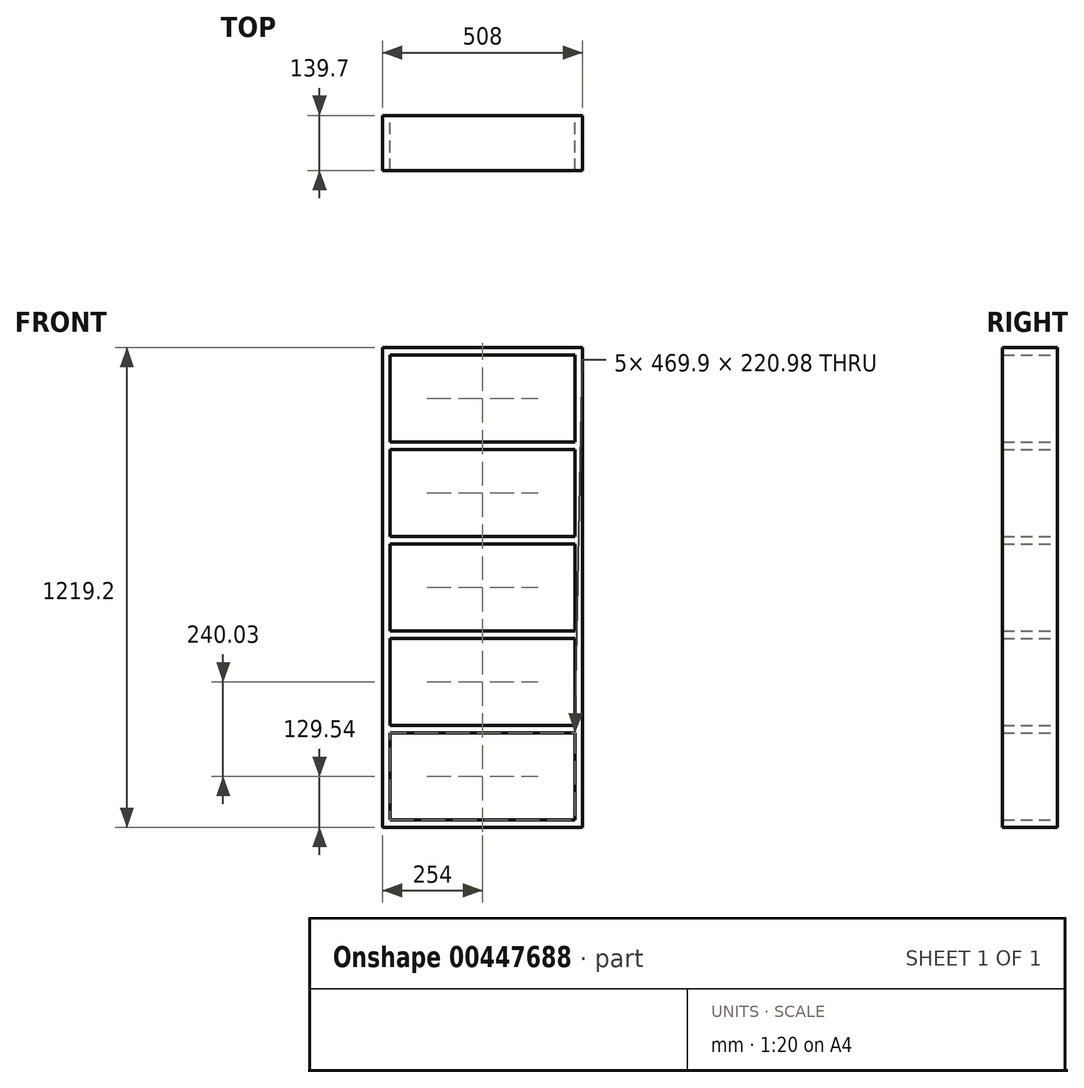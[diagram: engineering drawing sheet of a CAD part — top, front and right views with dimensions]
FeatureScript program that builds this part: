
annotation { "Feature Type Name" : "Feature", "Feature Type Description" : "" }
export const myFeature = defineFeature(function(context is Context, id is Id, definition is map)
    precondition{}
    {
        {
            var Q0;
            Q0=qCreatedBy(makeId("Front.planeOp"),FACE);
            var sketch = newSketch(context, id + "F0", { "sketchPlane" : qUnion([Q0])});
            skLineSegment(sketch, "E0.bottom", {"start": v(-254, 609.6) * mm, "end": v(254, 609.6) * mm});
            skLineSegment(sketch, "E0.top", {"start": v(-254, -609.6) * mm, "end": v(254, -609.6) * mm});
            skLineSegment(sketch, "E0.left", {"start": v(-254, 609.6) * mm, "end": v(-254, -609.6) * mm});
            skLineSegment(sketch, "E0.right", {"start": v(254, 609.6) * mm, "end": v(254, -609.6) * mm});
            skLineSegment(sketch, "E1.0", {"start": v(-234.95, 590.55) * mm, "end": v(234.95, 590.55) * mm});
            skLineSegment(sketch, "E2.0", {"start": v(234.95, 590.55) * mm, "end": v(234.95, -590.55) * mm});
            skLineSegment(sketch, "E3.0", {"start": v(-234.95, 590.55) * mm, "end": v(-234.95, -590.55) * mm});
            skLineSegment(sketch, "E4.0", {"start": v(-234.95, -590.55) * mm, "end": v(234.95, -590.55) * mm});
            skSolve(sketch);
        }
        {
            var Q0;
            Q0 = qSketchRegion(id + "F0", true);
            extrude(context, id + "F1", {"entities" : qUnion([Q0]), "depth" : 139.7 * mm});
        }
        {
            var Q0;
            Q0=qCreatedBy(makeId("Front.planeOp"),FACE);
            var sketch = newSketch(context, id + "F2", { "sketchPlane" : qUnion([Q0])});
            skLineSegment(sketch, "E5.bottom", {"start": v(-234.95, 369.57) * mm, "end": v(234.95, 369.57) * mm});
            skLineSegment(sketch, "E5.top", {"start": v(-234.95, 350.52) * mm, "end": v(234.95, 350.52) * mm});
            skLineSegment(sketch, "E5.left", {"start": v(-234.95, 369.57) * mm, "end": v(-234.95, 350.52) * mm});
            skLineSegment(sketch, "E5.right", {"start": v(234.95, 369.57) * mm, "end": v(234.95, 350.52) * mm});
            skLineSegment(sketch, "E6.bottom", {"start": v(-234.95, -110.49) * mm, "end": v(234.95, -110.49) * mm});
            skLineSegment(sketch, "E6.top", {"start": v(-234.95, -129.54) * mm, "end": v(234.95, -129.54) * mm});
            skLineSegment(sketch, "E6.left", {"start": v(-234.95, -110.49) * mm, "end": v(-234.95, -129.54) * mm});
            skLineSegment(sketch, "E6.right", {"start": v(234.95, -110.49) * mm, "end": v(234.95, -129.54) * mm});
            skLineSegment(sketch, "E7.bottom", {"start": v(-234.95, 129.54) * mm, "end": v(234.95, 129.54) * mm});
            skLineSegment(sketch, "E7.top", {"start": v(-234.95, 110.5) * mm, "end": v(234.95, 110.5) * mm});
            skLineSegment(sketch, "E7.left", {"start": v(-234.95, 129.54) * mm, "end": v(-234.95, 110.5) * mm});
            skLineSegment(sketch, "E7.right", {"start": v(234.95, 129.54) * mm, "end": v(234.95, 110.5) * mm});
            skLineSegment(sketch, "E8.bottom", {"start": v(-234.95, -350.52) * mm, "end": v(234.95, -350.52) * mm});
            skLineSegment(sketch, "E8.top", {"start": v(-234.95, -369.57) * mm, "end": v(234.95, -369.57) * mm});
            skLineSegment(sketch, "E8.left", {"start": v(-234.95, -350.52) * mm, "end": v(-234.95, -369.57) * mm});
            skLineSegment(sketch, "E8.right", {"start": v(234.95, -350.52) * mm, "end": v(234.95, -369.57) * mm});
            skLineSegment(sketch, "E9", {"start": v(0, 369.57) * mm, "end": v(0, 590.55) * mm, "construction": true});
            skPoint(sketch, "E9.endSnap0", {"position": v(0, 369.57) * mm});
            skLineSegment(sketch, "E10", {"start": v(0, 350.52) * mm, "end": v(0, 129.54) * mm, "construction": true});
            skLineSegment(sketch, "E11", {"start": v(0, 110.5) * mm, "end": v(0, -110.49) * mm, "construction": true});
            skLineSegment(sketch, "E12", {"start": v(0, -129.54) * mm, "end": v(0, -350.52) * mm, "construction": true});
            skLineSegment(sketch, "E13", {"start": v(0, -369.57) * mm, "end": v(0, -590.55) * mm, "construction": true});
            skSolve(sketch);
        }
        {
            var Q0;
            Q0 = qSketchRegion(id + "F2", true);
            extrude(context, id + "F3", {"entities" : qUnion([Q0]), "operationType" : NewBodyOperationType.ADD, "depth" : 139.7 * mm});
        }
    });
